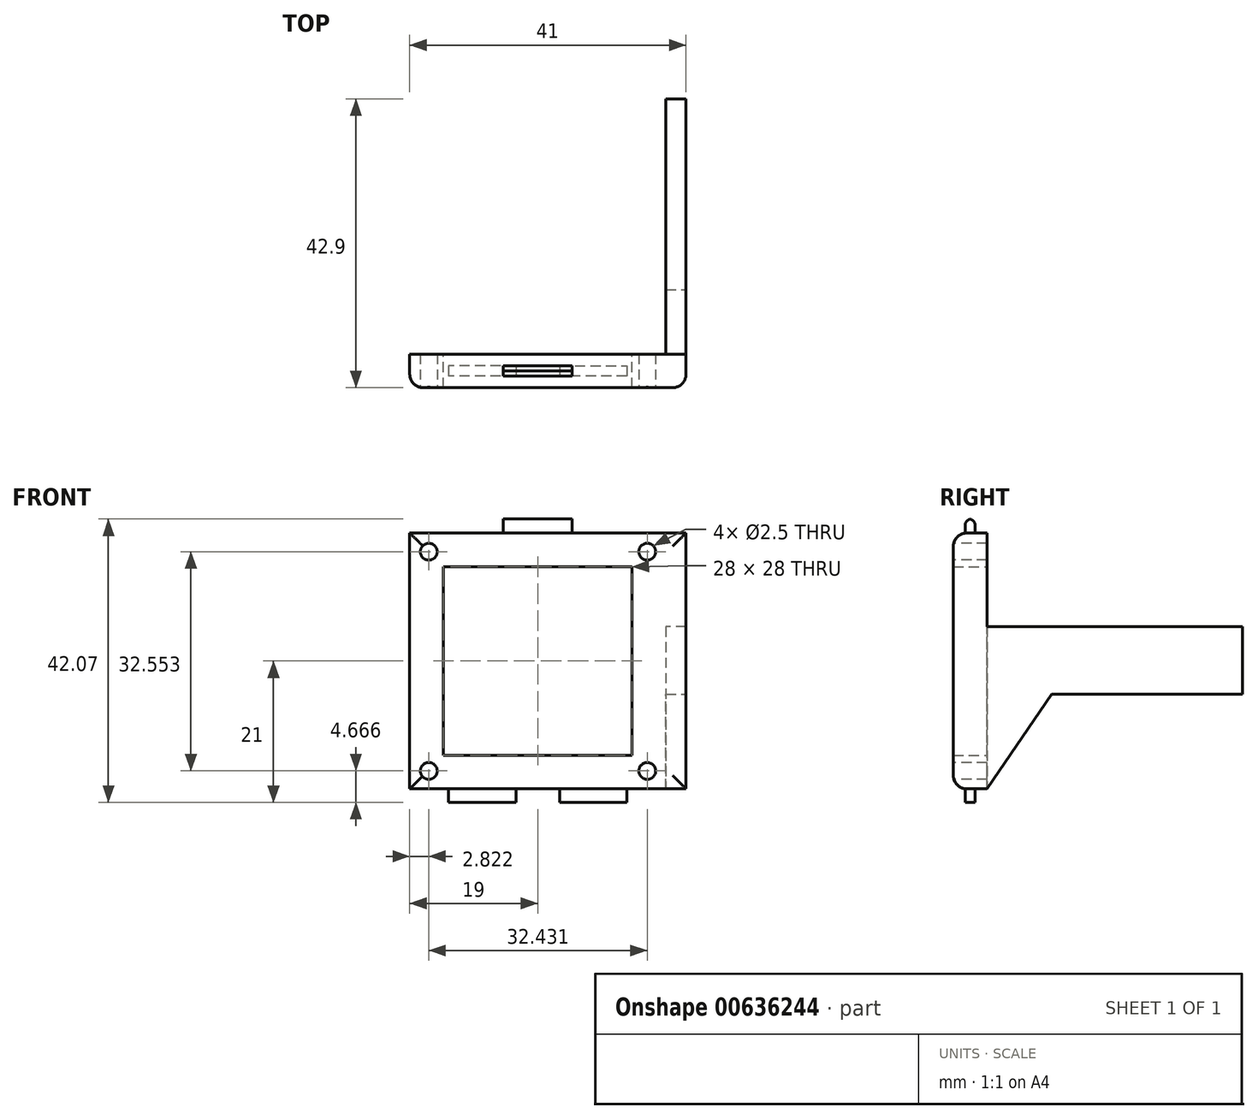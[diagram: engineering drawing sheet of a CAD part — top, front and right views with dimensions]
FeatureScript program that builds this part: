
annotation { "Feature Type Name" : "Feature", "Feature Type Description" : "" }
export const myFeature = defineFeature(function(context is Context, id is Id, definition is map)
    precondition{}
    {
        {
            var Q0;
            Q0=qCreatedBy(makeId("Front.planeOp"),FACE);
            var sketch = newSketch(context, id + "F0", { "sketchPlane" : qUnion([Q0])});
            skLineSegment(sketch, "E0.bottom", {"start": v(19, -19) * mm, "end": v(-19, -19) * mm});
            skLineSegment(sketch, "E0.top", {"start": v(19, 19) * mm, "end": v(-19, 19) * mm});
            skLineSegment(sketch, "E0.left", {"start": v(19, -19) * mm, "end": v(19, 19) * mm});
            skLineSegment(sketch, "E0.right", {"start": v(-19, -19) * mm, "end": v(-19, 19) * mm});
            skPoint(sketch, "E0.middle", {"position": v(0, 0) * mm});
            skLineSegment(sketch, "E1.bottom", {"start": v(14, -14) * mm, "end": v(-14, -14) * mm});
            skLineSegment(sketch, "E1.top", {"start": v(14, 14) * mm, "end": v(-14, 14) * mm});
            skLineSegment(sketch, "E1.left", {"start": v(14, -14) * mm, "end": v(14, 14) * mm});
            skLineSegment(sketch, "E1.right", {"start": v(-14, -14) * mm, "end": v(-14, 14) * mm});
            skSolve(sketch);
        }
        {
            var Q0;
            Q0=makeQuery(id+"F0.imprint","IMPRINT",FACE,{"disambiguationData":[TD([[makeQuery(id+"F0.imprint","IMPRINT",EDGE,{"derivedFrom":sQuery(id+"F0.wireOp",EDGE,"E0.bottom")}),-1.0]])]});
            extrude(context, id + "F1", {"entities" : qUnion([Q0]), "depth" : 5 * mm, "offsetDistance" : 25 * mm});
        }
        {
            var Q0;
            Q0=makeQuery(id+"F1.opExtrude","SWEPT_FACE",FACE,{"disambiguationData":[OSD([sQuery(id+"F0.wireOp",EDGE,"E0.top")])]});
            var sketch = newSketch(context, id + "F2", { "sketchPlane" : qUnion([Q0])});
            skLineSegment(sketch, "E2.bottom", {"start": v(5.1, -1.75) * mm, "end": v(-5.1, -1.75) * mm});
            skLineSegment(sketch, "E2.top", {"start": v(5.1, -3.25) * mm, "end": v(-5.1, -3.25) * mm});
            skLineSegment(sketch, "E2.left", {"start": v(5.1, -1.75) * mm, "end": v(5.1, -3.25) * mm});
            skLineSegment(sketch, "E2.right", {"start": v(-5.1, -1.75) * mm, "end": v(-5.1, -3.25) * mm});
            skPoint(sketch, "E2.middle", {"position": v(0, -2.5) * mm});
            skPoint(sketch, "E2.middle.positionSnap0", {"position": v(-19, -2.5) * mm});
            skPoint(sketch, "E2.centerSnap0", {"position": v(-19, -2.5) * mm});
            skSolve(sketch);
        }
        {
            var Q0;
            Q0=makeQuery(id+"F2.imprint","IMPRINT",FACE,{"disambiguationData":[TD([[makeQuery(id+"F2.imprint","IMPRINT",EDGE,{"derivedFrom":sQuery(id+"F2.wireOp",EDGE,"E2.bottom")}),1.0]])]});
            extrude(context, id + "F3", {"entities" : qUnion([Q0]), "operationType" : NewBodyOperationType.ADD, "depth" : 2.1 * mm, "offsetDistance" : 25 * mm});
        }
        {
            var Q0;
            Q0=makeQuery(id+"F3.opExtrude","CAP_EDGE",EDGE,{"disambiguationData":[OSD([sQuery(id+"F2.wireOp",EDGE,"E2.top")])],"isStart":false});
            var Q1;
            Q1=makeQuery(id+"F3.opExtrude","CAP_EDGE",EDGE,{"disambiguationData":[OSD([sQuery(id+"F2.wireOp",EDGE,"E2.bottom")])],"isStart":false});
            fillet(context, id + "F4", {"entities" : qUnion([Q0, Q1]), "radius" : 1 * mm, "tangentPropagation" : true, "allowEdgeOverflow" : false});
        }
        {
            var Q0;
            Q0=makeQuery(id+"F1.opExtrude","SWEPT_FACE",FACE,{"disambiguationData":[OSD([sQuery(id+"F0.wireOp",EDGE,"E0.bottom")])]});
            var sketch = newSketch(context, id + "F5", { "sketchPlane" : qUnion([Q0])});
            skLineSegment(sketch, "E3", {"start": v(-19, 2.5) * mm, "end": v(19, 2.5) * mm, "construction": true});
            skLineSegment(sketch, "E4", {"start": v(0, 5) * mm, "end": v(0, 0) * mm, "construction": true});
            skLineSegment(sketch, "E5", {"start": v(0, 0) * mm, "end": v(-19, 5) * mm, "construction": true});
            skLineSegment(sketch, "E6", {"start": v(0, 0) * mm, "end": v(19, 5) * mm, "construction": true});
            skPoint(sketch, "E7.middle", {"position": v(9.5, 2.5) * mm});
            skLineSegment(sketch, "E8.bottom", {"start": v(-3.23, 1.75) * mm, "end": v(-15.78, 1.75) * mm});
            skLineSegment(sketch, "E8.top", {"start": v(-3.23, 3.25) * mm, "end": v(-15.78, 3.25) * mm});
            skLineSegment(sketch, "E8.left", {"start": v(-3.23, 1.75) * mm, "end": v(-3.23, 3.25) * mm});
            skLineSegment(sketch, "E8.right", {"start": v(-13.23, 1.75) * mm, "end": v(-13.23, 3.25) * mm});
            skPoint(sketch, "E8.middle", {"position": v(-9.5, 2.5) * mm});
            skLineSegment(sketch, "E9.MirrorCS", {"start": v(3.23, 1.75) * mm, "end": v(15.78, 1.75) * mm});
            skLineSegment(sketch, "E10.MirrorCS", {"start": v(13.23, 1.75) * mm, "end": v(13.23, 3.25) * mm});
            skLineSegment(sketch, "E11.MirrorCS", {"start": v(3.23, 3.25) * mm, "end": v(15.78, 3.25) * mm});
            skLineSegment(sketch, "E12.MirrorCS", {"start": v(3.23, 1.75) * mm, "end": v(3.23, 3.25) * mm});
            skSolve(sketch);
        }
        {
            var Q0;
            Q0=makeQuery(id+"F5.imprint","IMPRINT",FACE,{"disambiguationData":[TD([[makeQuery(id+"F5.imprint","IMPRINT",EDGE,{"derivedFrom":sQuery(id+"F5.wireOp",EDGE,"E8.bottom")}),-1.0]])]});
            var Q1;
            Q1=makeQuery(id+"F5.imprint","IMPRINT",FACE,{"disambiguationData":[TD([[makeQuery(id+"F5.imprint","IMPRINT",EDGE,{"derivedFrom":sQuery(id+"F5.wireOp",EDGE,"E9.MirrorCS")}),1.0]])]});
            extrude(context, id + "F6", {"entities" : qUnion([Q0, Q1]), "operationType" : NewBodyOperationType.ADD, "depth" : 2 * mm, "offsetDistance" : 25 * mm});
        }
        {
            var Q0;
            Q0=makeQuery(id+"F1.opExtrude","CAP_FACE",FACE,{"disambiguationData":[OSD([sQuery(id+"F0.wireOp",EDGE,"E0.bottom"),sQuery(id+"F0.wireOp",EDGE,"E0.top"),sQuery(id+"F0.wireOp",EDGE,"E0.left"),sQuery(id+"F0.wireOp",EDGE,"E0.right"),sQuery(id+"F0.wireOp",EDGE,"E1.bottom"),sQuery(id+"F0.wireOp",EDGE,"E1.top"),sQuery(id+"F0.wireOp",EDGE,"E1.left"),sQuery(id+"F0.wireOp",EDGE,"E1.right")])],"isStart":false});
            var sketch = newSketch(context, id + "F7", { "sketchPlane" : qUnion([Q0])});
            skPoint(sketch, "E13", {"position": v(-16.18, 16.22) * mm});
            skPoint(sketch, "E14", {"position": v(-16.18, -16.33) * mm});
            skPoint(sketch, "E15", {"position": v(16.25, -16.33) * mm});
            skPoint(sketch, "E16", {"position": v(16.25, 16.22) * mm});
            skSolve(sketch);
        }
        {
            var Q0;
            Q0=sQuery(id+"F7.wireOp",VERTEX,"E16");
            var Q1;
            Q1=sQuery(id+"F7.wireOp",VERTEX,"E13");
            var Q2;
            Q2=sQuery(id+"F7.wireOp",VERTEX,"E14");
            var Q3;
            Q3=sQuery(id+"F7.wireOp",VERTEX,"E15");
            var Q4;
            Q4=makeQuery(id+"F1.opExtrude","SWEPT_BODY",BODY,{"disambiguationData":[OSD([sQuery(id+"F0.wireOp",EDGE,"E0.bottom"),sQuery(id+"F0.wireOp",EDGE,"E0.top"),sQuery(id+"F0.wireOp",EDGE,"E0.left"),sQuery(id+"F0.wireOp",EDGE,"E0.right"),sQuery(id+"F0.wireOp",EDGE,"E1.bottom"),sQuery(id+"F0.wireOp",EDGE,"E1.top"),sQuery(id+"F0.wireOp",EDGE,"E1.left"),sQuery(id+"F0.wireOp",EDGE,"E1.right")])]});
            hole(context, id + "F8", {"style" : HoleStyle.SIMPLE, "endStyle" : HoleEndStyle.THROUGH, "holeDiameter" : 2.5 * mm, "majorDiameter" : 5 * mm, "isTappedThrough" : true, "tappedDepth" : 12 * mm, "tapClearance" : 3, "locations" : qUnion([Q0, Q1, Q2, Q3]), "scope" : qUnion([Q4])});
        }
        {
            var Q0;
            Q0=makeQuery(id+"F1.opExtrude","SWEPT_FACE",FACE,{"disambiguationData":[OSD([sQuery(id+"F0.wireOp",EDGE,"E0.left")])]});
            extrude(context, id + "F9", {"entities" : qUnion([Q0]), "operationType" : NewBodyOperationType.ADD, "depth" : 3 * mm, "offsetDistance" : 25 * mm});
        }
        {
            var Q0;
            {var subQ0=sQuery(id+"F0.wireOp",EDGE,"E0.left");Q0=makeQuery(id+"F9.boolean.opBoolean","MERGE",FACE,{"derivedFrom":[makeQuery(id+"F1.opExtrude","CAP_FACE",FACE,{"disambiguationData":[OSD([sQuery(id+"F0.wireOp",EDGE,"E0.bottom"),sQuery(id+"F0.wireOp",EDGE,"E0.top"),subQ0,sQuery(id+"F0.wireOp",EDGE,"E0.right"),sQuery(id+"F0.wireOp",EDGE,"E1.bottom"),sQuery(id+"F0.wireOp",EDGE,"E1.top"),sQuery(id+"F0.wireOp",EDGE,"E1.left"),sQuery(id+"F0.wireOp",EDGE,"E1.right")])],"isStart":true}),makeQuery(id+"F9.opExtrude","SWEPT_FACE",FACE,{"disambiguationData":[OSD([subQ0]),TDD([makeQuery(id+"F1.opExtrude","CAP_EDGE",EDGE,{"disambiguationData":[OSD([subQ0])],"isStart":true})])]})]});}
            var sketch = newSketch(context, id + "F10", { "sketchPlane" : qUnion([Q0])});
            skLineSegment(sketch, "E17.bottom", {"start": v(-22, 5.08) * mm, "end": v(-19, 5.08) * mm});
            skLineSegment(sketch, "E17.top", {"start": v(-22, -4.92) * mm, "end": v(-19, -4.92) * mm});
            skLineSegment(sketch, "E17.left", {"start": v(-22, 5.08) * mm, "end": v(-22, -4.92) * mm});
            skLineSegment(sketch, "E17.right", {"start": v(-19, 5.08) * mm, "end": v(-19, -4.92) * mm});
            skSolve(sketch);
        }
        {
            var Q0;
            Q0=makeQuery(id+"F10.imprint","IMPRINT",FACE,{"disambiguationData":[TD([[makeQuery(id+"F10.imprint","IMPRINT",EDGE,{"derivedFrom":sQuery(id+"F10.wireOp",EDGE,"E17.bottom")}),-1.0]])]});
            extrude(context, id + "F11", {"entities" : qUnion([Q0]), "operationType" : NewBodyOperationType.ADD, "depth" : 37.9 * mm, "offsetDistance" : 25 * mm});
        }
        {
            var Q0;
            Q0=makeQuery(id+"F11.boolean.opBoolean","MERGE",FACE,{"derivedFrom":[makeQuery(id+"F9.opExtrude","CAP_FACE",FACE,{"disambiguationData":[OSD([sQuery(id+"F0.wireOp",EDGE,"E0.left")])],"isStart":false}),makeQuery(id+"F11.opExtrude","SWEPT_FACE",FACE,{"disambiguationData":[OSD([sQuery(id+"F10.wireOp",EDGE,"E17.left")])]})]});
            var sketch = newSketch(context, id + "F12", { "sketchPlane" : qUnion([Q0])});
            skLineSegment(sketch, "E18", {"start": v(0, -19) * mm, "end": v(9.57, -4.92) * mm});
            skSolve(sketch);
        }
        {
            var Q0;
            {var subQ0=sQuery(id+"F12.wireOp",EDGE,"E18");Q0=makeQuery(id+"F12.imprint","IMPRINT",FACE,{"disambiguationData":[TD([[makeQuery(id+"F12.imprint","IMPRINT",EDGE,{"derivedFrom":subQ0}),1.0]])]});}
            var Q1;
            Q1=makeQuery(id+"F11.opExtrude","SWEPT_FACE",FACE,{"disambiguationData":[OSD([sQuery(id+"F10.wireOp",EDGE,"E17.right")])]});
            extrude(context, id + "F13", {"entities" : qUnion([Q0]), "operationType" : NewBodyOperationType.ADD, "endBound" : BoundingType.UP_TO_SURFACE, "oppositeDirection" : true, "depth" : 25 * mm, "endBoundEntityFace" : qUnion([Q1]), "offsetDistance" : 25 * mm});
        }
        {
            var Q0;
            {var subQ0=sQuery(id+"F0.wireOp",EDGE,"E0.left");Q0=makeQuery(id+"F9.opExtrude","CAP_EDGE",EDGE,{"disambiguationData":[OSD([subQ0]),TDD([makeQuery(id+"F1.opExtrude","CAP_EDGE",EDGE,{"disambiguationData":[OSD([subQ0])],"isStart":false})])],"isStart":false});}
            var Q1;
            {var subQ0=sQuery(id+"F0.wireOp",EDGE,"E0.left");var subQ1=sQuery(id+"F0.wireOp",EDGE,"E0.top");Q1=makeQuery(id+"F9.boolean.opBoolean","MERGE",EDGE,{"derivedFrom":[makeQuery(id+"F1.opExtrude","CAP_EDGE",EDGE,{"disambiguationData":[OSD([subQ1])],"isStart":false}),makeQuery(id+"F9.opExtrude","SWEPT_EDGE",EDGE,{"disambiguationData":[OSD([subQ1,subQ0]),TDD([makeQuery(id+"F1.opExtrude","CAP_VERTEX",VERTEX,{"disambiguationData":[OSD([subQ1,subQ0])],"isStart":false})])]})]});}
            var Q2;
            Q2=makeQuery(id+"F1.opExtrude","CAP_EDGE",EDGE,{"disambiguationData":[OSD([sQuery(id+"F0.wireOp",EDGE,"E0.right")])],"isStart":false});
            var Q3;
            {var subQ0=sQuery(id+"F0.wireOp",EDGE,"E0.left");var subQ1=sQuery(id+"F0.wireOp",EDGE,"E0.bottom");Q3=makeQuery(id+"F9.boolean.opBoolean","MERGE",EDGE,{"derivedFrom":[makeQuery(id+"F1.opExtrude","CAP_EDGE",EDGE,{"disambiguationData":[OSD([subQ1])],"isStart":false}),makeQuery(id+"F9.opExtrude","SWEPT_EDGE",EDGE,{"disambiguationData":[OSD([subQ1,subQ0]),TDD([makeQuery(id+"F1.opExtrude","CAP_VERTEX",VERTEX,{"disambiguationData":[OSD([subQ1,subQ0])],"isStart":false})])]})]});}
            fillet(context, id + "F14", {"entities" : qUnion([Q0, Q1, Q2, Q3]), "radius" : 2 * mm, "tangentPropagation" : true, "allowEdgeOverflow" : false});
        }
    });
